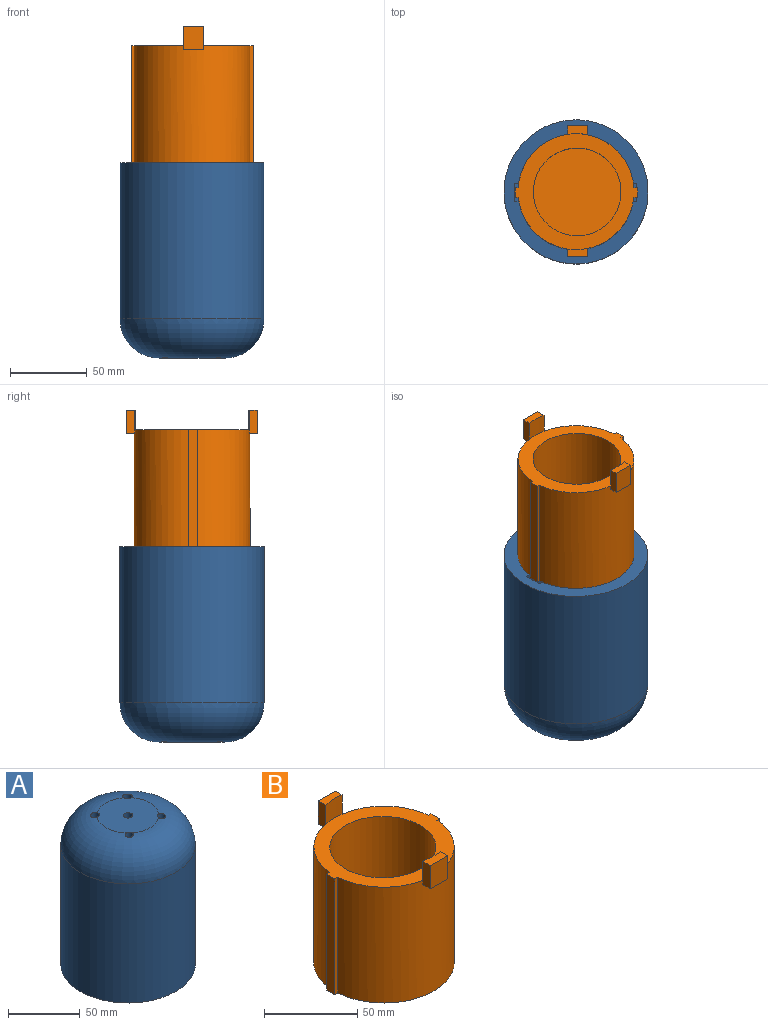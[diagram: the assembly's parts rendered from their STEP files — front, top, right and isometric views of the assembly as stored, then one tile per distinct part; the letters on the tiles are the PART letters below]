
ASSEMBLY  parts=2 mates=1
PART A: 19 faces, bbox 93.7x93.7x127 mm
  f0: plane 42.9x42.9mm, normal (0,0,1), area 1394.8mm2, adj f4,f14,f15,f16,f17,f18
  f1: plane 93.7x93.7mm, normal (0,0,-1), area 2707.8mm2, adj f2,f3,f7,f8,f9,f11,f12,f13
  f2: cylinder r=36.14mm len=101.6mm, axis (0,0,-1), area 21277.4mm2, adj f1,f5,f6,f7,f8,f10,f12,f13
  f3: cylinder r=46.85mm len=101.6mm, axis (0,0,-1), area 29907.4mm2, adj f1,f4
  f4: torus R=21.45mm, axis (0,0,1), area 9333.3mm2, adj f0,f3,f14,f15,f16,f17
  f5: plane 72.28x72.28mm, normal (0,0,-1), area 3955.7mm2, adj f2,f14,f15,f16,f17,f18
  f6: plane 11.72x4.25mm, normal (0,0,-1), area 45.5mm2, adj f2,f7,f8,f9
  f7: plane 76.2x4.15mm, normal (0,-1,0), area 316.5mm2, adj f1,f2,f6,f9
  f8: plane 76.2x4.25mm, normal (0,1,0), area 323.7mm2, adj f1,f2,f6,f9
  f9: plane 76.2x11.72mm, normal (-1,0,0), area 892.7mm2, adj f1,f6,f7,f8
  f10: plane 11.72x3.68mm, normal (0,0,-1), area 38.8mm2, adj f2,f11,f12,f13
  f11: plane 76.2x11.72mm, normal (1,0,0), area 892.7mm2, adj f1,f10,f12,f13
  f12: plane 76.2x3.68mm, normal (0,1,0), area 280.1mm2, adj f1,f2,f10,f11
  f13: plane 76.2x3.58mm, normal (0,-1,0), area 273mm2, adj f1,f2,f10,f11
  f14: cylinder r=2.77mm len=25.4mm, axis (0,0,-1), area 438.8mm2, adj f0,f4,f5
  f15: cylinder r=2.89mm len=25.4mm, axis (0,0,-1), area 458.6mm2, adj f0,f4,f5
  f16: cylinder r=3.3mm len=25.4mm, axis (0,0,-1), area 523mm2, adj f0,f4,f5
  f17: cylinder r=3.06mm len=25.4mm, axis (0,0,-1), area 486.2mm2, adj f0,f4,f5
  f18: cylinder r=3.27mm len=25.4mm, axis (0,0,-1), area 521.8mm2, adj f0,f5
PART B: 24 faces, bbox 79.4x85.2x88.9 mm
  f0: cylinder r=37.72mm len=76.2mm, axis (0,0,-1), area 8604.9mm2, adj f3,f4,f6,f9,f19,f21,f23
  f1: cylinder r=37.72mm len=76.2mm, axis (0,0,-1), area 8430.1mm2, adj f3,f4,f5,f8,f14,f15,f17
  f2: cylinder r=28.54mm len=71.12mm, axis (0,0,-1), area 12751.8mm2, adj f3,f11
  f3: plane 79.37x75.45mm, normal (0,0,1), area 1937.5mm2, adj f0,f1,f2,f5,f6,f7,f8,f9
  f4: plane 79.37x75.45mm, normal (0,0,-1), area 4495.8mm2, adj f0,f1,f5,f6,f7,f8,f9,f10
  f5: plane 76.2x2.42mm, normal (0,1,0), area 184.3mm2, adj f1,f3,f4,f7
  f6: plane 76.2x2.32mm, normal (0,-1,0), area 177mm2, adj f0,f3,f4,f7
  f7: plane 76.2x6.29mm, normal (-1,0,0), area 479mm2, adj f3,f4,f5,f6
  f8: plane 76.2x1.88mm, normal (0,1,0), area 143.1mm2, adj f1,f3,f4,f10
  f9: plane 76.2x1.78mm, normal (0,-1,0), area 135.8mm2, adj f0,f3,f4,f10
  f10: plane 76.2x6.29mm, normal (1,0,0), area 479mm2, adj f3,f4,f8,f9
  f11: plane 57.07x57.07mm, normal (0,0,1), area 2558.3mm2, adj f2
  f12: cylinder r=37.72mm len=13.02mm, axis (0,0,-1), area 166.3mm2, adj f3,f14,f15,f16
  f13: plane 15.24x13.02mm, normal (0,1,0), area 198.5mm2, adj f14,f15,f16,f17
  f14: plane 15.24x5.49mm, normal (-1,0,0), area 83.7mm2, adj f1,f12,f13,f16,f17
  f15: plane 15.24x5.11mm, normal (1,0,0), area 77.9mm2, adj f1,f12,f13,f16,f17
  f16: plane 13.02x5.49mm, normal (0,0,1), area 64.1mm2, adj f12,f13,f14,f15
  f17: plane 13.02x5.49mm, normal (0,0,-1), area 64.1mm2, adj f1,f13,f14,f15
  f18: cylinder r=37.72mm len=13.02mm, axis (0,0,-1), area 166.3mm2, adj f3,f19,f21,f22
  f19: plane 15.24x5.86mm, normal (-1,0,0), area 89.3mm2, adj f0,f18,f20,f22,f23
  f20: plane 15.24x13.02mm, normal (0,-1,0), area 198.5mm2, adj f19,f21,f22,f23
  f21: plane 15.24x5.48mm, normal (1,0,0), area 83.5mm2, adj f0,f18,f20,f22,f23
  f22: plane 13.02x5.86mm, normal (0,0,1), area 68.9mm2, adj f18,f19,f20,f21
  f23: plane 13.02x5.86mm, normal (0,0,-1), area 68.9mm2, adj f0,f19,f20,f21
PLACE A rot(axis=(0,1,0),180deg) t=(-54.76,28.52,242.2)mm
PLACE B rot(axis=(0,0,1),180deg) t=(-54.05,28.38,242.2)mm
MATE slider B.f0 <-> A.f2  axis (0,0,-1) through (-54.76,28.52,242.2)mm
